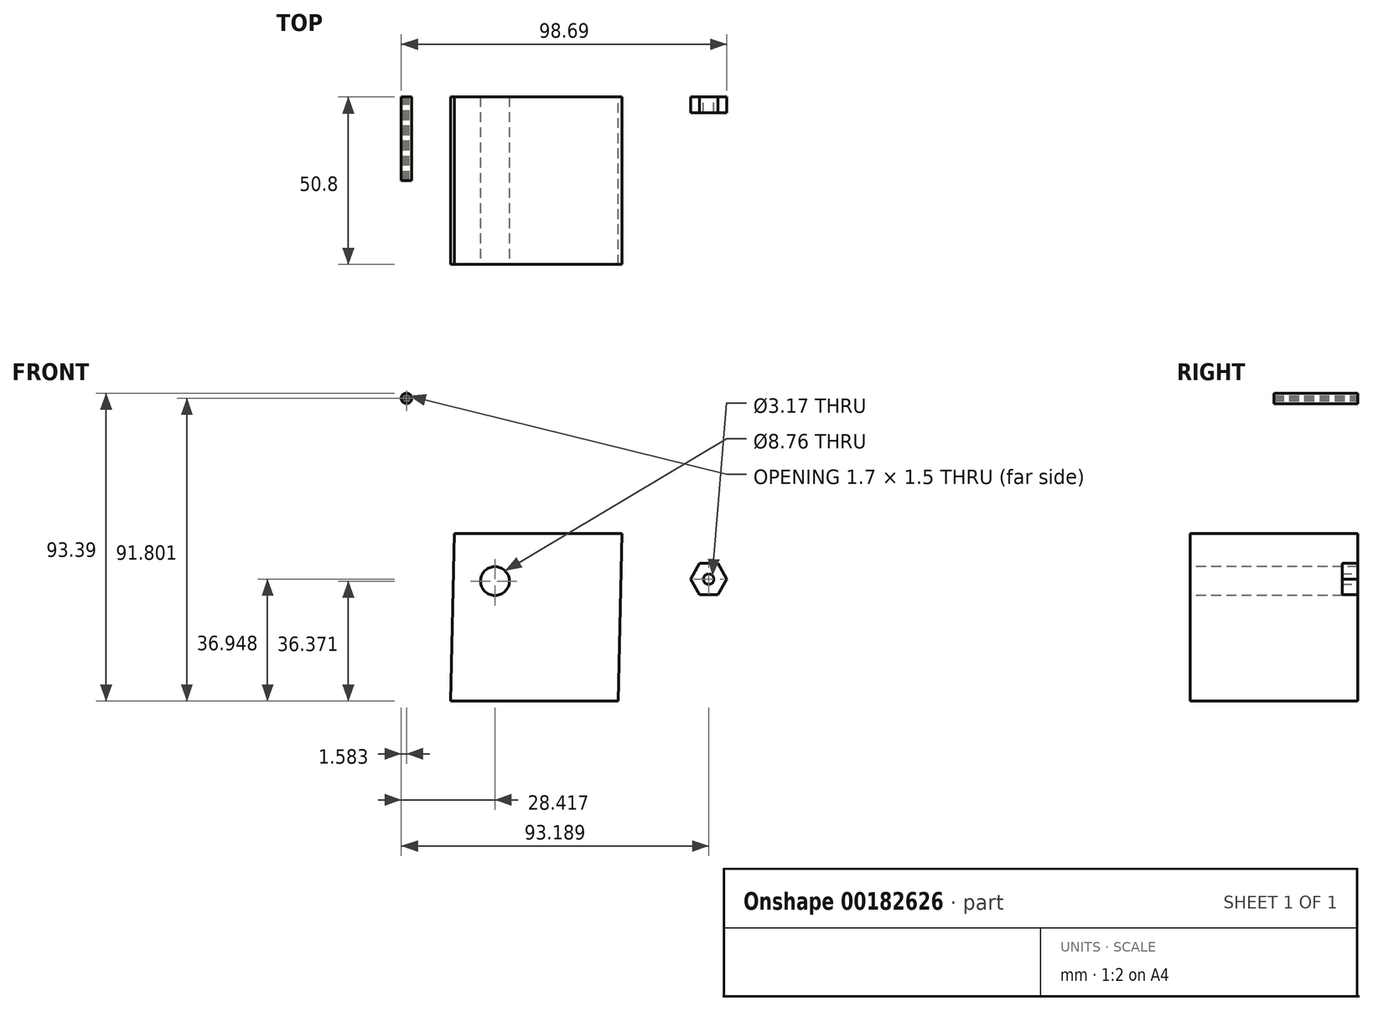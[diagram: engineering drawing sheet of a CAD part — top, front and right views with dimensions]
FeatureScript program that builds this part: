
annotation { "Feature Type Name" : "Feature", "Feature Type Description" : "" }
export const myFeature = defineFeature(function(context is Context, id is Id, definition is map)
    precondition{}
    {
        {
            var Q0;
            Q0=qCreatedBy(makeId("Front.planeOp"),FACE);
            var sketch = newSketch(context, id + "F0", { "sketchPlane" : qUnion([Q0])});
            skLineSegment(sketch, "E0", {"start": v(-36.1, 20.97) * mm, "end": v(14.7, 20.97) * mm});
            skLineSegment(sketch, "E1", {"start": v(14.7, 20.97) * mm, "end": v(13.52, -29.81) * mm});
            skLineSegment(sketch, "E2", {"start": v(13.52, -29.81) * mm, "end": v(-37.28, -29.81) * mm});
            skLineSegment(sketch, "E3", {"start": v(-37.28, -29.81) * mm, "end": v(-36.1, 20.97) * mm});
            skSolve(sketch);
        }
        {
            var Q0;
            Q0=makeQuery(id+"F0.imprint","IMPRINT",FACE,{"disambiguationData":[TD([[makeQuery(id+"F0.imprint","IMPRINT",EDGE,{"derivedFrom":sQuery(id+"F0.wireOp",EDGE,"E0")}),-1.0]])]});
            extrude(context, id + "F1", {"entities" : qUnion([Q0]), "depth" : 50.8 * mm});
        }
        {
            var Q0;
            Q0=makeQuery(id+"F1.opExtrude","CAP_FACE",FACE,{"disambiguationData":[OSD([sQuery(id+"F0.wireOp",EDGE,"E0"),sQuery(id+"F0.wireOp",EDGE,"E1"),sQuery(id+"F0.wireOp",EDGE,"E2"),sQuery(id+"F0.wireOp",EDGE,"E3")])],"isStart":false});
            var sketch = newSketch(context, id + "F2", { "sketchPlane" : qUnion([Q0])});
            skCircle(sketch, "E4", {"center": v(-23.78, 6.56) * mm, "radius": 4.38 * mm});
            skSolve(sketch);
        }
        {
            var Q0;
            Q0=makeQuery(id+"F2.imprint","IMPRINT",FACE,{"disambiguationData":[TD([[makeQuery(id+"F2.imprint","IMPRINT",EDGE,{"derivedFrom":sQuery(id+"F2.wireOp",EDGE,"E4")}),1.0]])]});
            extrude(context, id + "F3", {"entities" : qUnion([Q0]), "operationType" : NewBodyOperationType.REMOVE, "oppositeDirection" : true, "depth" : 50.8 * mm});
        }
        {
            var Q0;
            Q0=qCreatedBy(makeId("Front.planeOp"),FACE);
            var sketch = newSketch(context, id + "F4", { "sketchPlane" : qUnion([Q0])});
            skCircle(sketch, "E5.cCircle", {"center": v(40.99, 7.14) * mm, "radius": 4.76 * mm, "construction": true});
            skLineSegment(sketch, "E5.0", {"start": v(43.74, 2.38) * mm, "end": v(38.24, 2.38) * mm});
            skLineSegment(sketch, "E5.1", {"start": v(38.24, 2.38) * mm, "end": v(35.49, 7.14) * mm});
            skLineSegment(sketch, "E5.2", {"start": v(35.49, 7.14) * mm, "end": v(38.24, 11.9) * mm});
            skLineSegment(sketch, "E5.3", {"start": v(38.24, 11.9) * mm, "end": v(43.74, 11.9) * mm});
            skLineSegment(sketch, "E5.4", {"start": v(43.74, 11.9) * mm, "end": v(46.49, 7.14) * mm});
            skLineSegment(sketch, "E5.5", {"start": v(46.49, 7.14) * mm, "end": v(43.74, 2.38) * mm});
            skPoint(sketch, "E5.0.midPoint", {"position": v(40.99, 2.38) * mm});
            skCircle(sketch, "E6", {"center": v(40.99, 7.14) * mm, "radius": 1.59 * mm});
            skSolve(sketch);
        }
        {
            var Q0;
            Q0 = qSketchRegion(id + "F4", true);
            extrude(context, id + "F5", {"entities" : qUnion([Q0]), "depth" : 4.76 * mm});
        }
        {
            var Q0;
            Q0=qCreatedBy(makeId("Front.planeOp"),FACE);
            var sketch = newSketch(context, id + "F6", { "sketchPlane" : qUnion([Q0])});
            skCircle(sketch, "E7", {"center": v(-50.62, 62) * mm, "radius": 1.59 * mm});
            skCircle(sketch, "E8.cCircle", {"center": v(-50.62, 62) * mm, "radius": 0.73 * mm, "construction": true});
            skLineSegment(sketch, "E8.0", {"start": v(-51.04, 62.73) * mm, "end": v(-50.2, 62.73) * mm});
            skLineSegment(sketch, "E8.1", {"start": v(-50.2, 62.73) * mm, "end": v(-49.77, 62) * mm});
            skLineSegment(sketch, "E8.2", {"start": v(-49.77, 62) * mm, "end": v(-50.2, 61.26) * mm});
            skLineSegment(sketch, "E8.3", {"start": v(-50.2, 61.26) * mm, "end": v(-51.04, 61.26) * mm});
            skLineSegment(sketch, "E8.4", {"start": v(-51.04, 61.26) * mm, "end": v(-51.46, 62) * mm});
            skLineSegment(sketch, "E8.5", {"start": v(-51.46, 62) * mm, "end": v(-51.04, 62.73) * mm});
            skPoint(sketch, "E8.0.midPoint", {"position": v(-50.62, 62.73) * mm});
            skCircle(sketch, "E9", {"center": v(-50.62, 62) * mm, "radius": 0.75 * mm});
            skSolve(sketch);
        }
        {
            var Q0;
            Q0=makeQuery(id+"F6.imprint","IMPRINT",FACE,{"disambiguationData":[TD([[makeQuery(id+"F6.imprint","IMPRINT",EDGE,{"derivedFrom":sQuery(id+"F6.wireOp",EDGE,"E7")}),1.0]])]});
            extrude(context, id + "F7", {"entities" : qUnion([Q0]), "depth" : 25.4 * mm});
        }
    });
